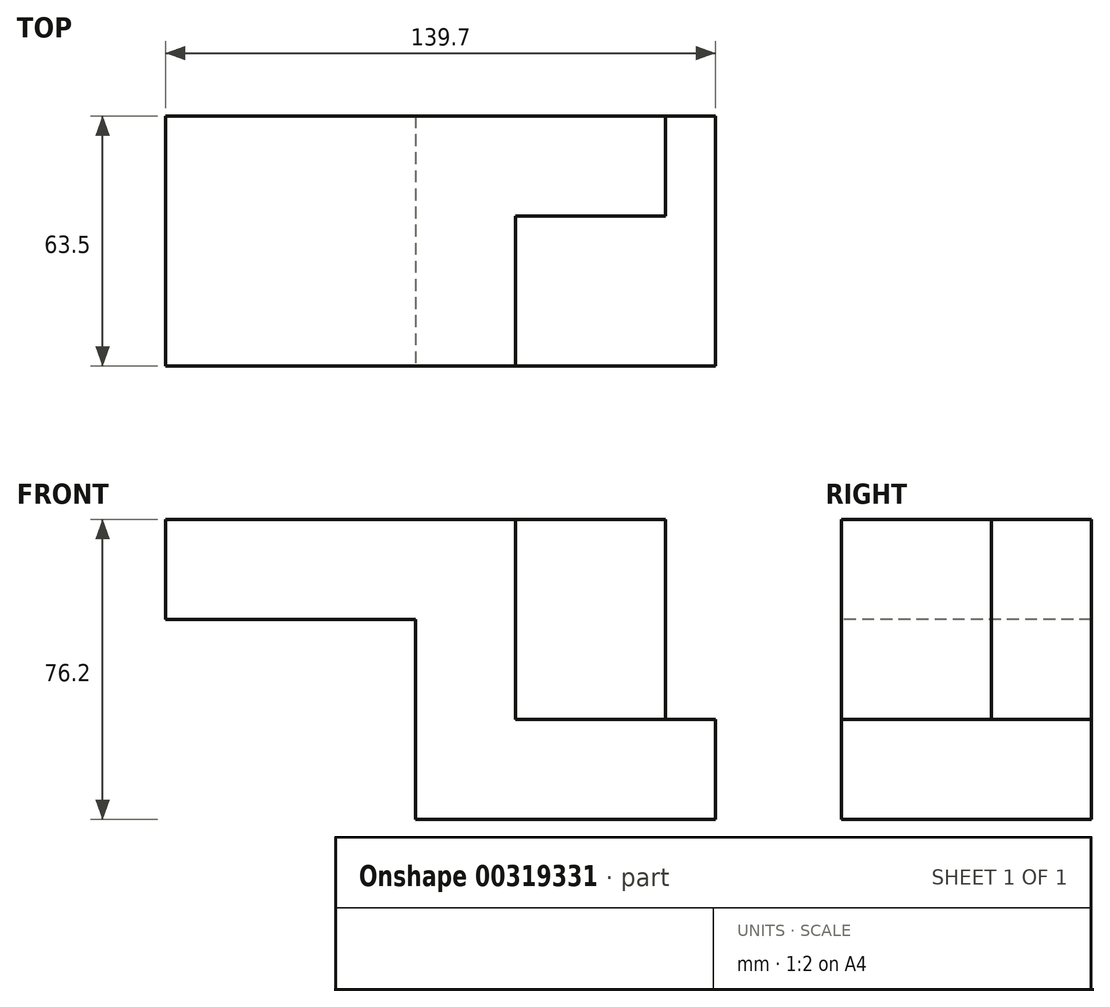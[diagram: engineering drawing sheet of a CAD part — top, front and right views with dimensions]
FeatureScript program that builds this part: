
annotation { "Feature Type Name" : "Feature", "Feature Type Description" : "" }
export const myFeature = defineFeature(function(context is Context, id is Id, definition is map)
    precondition{}
    {
        {
            var Q0;
            Q0=qCreatedBy(makeId("Top.planeOp"),FACE);
            var sketch = newSketch(context, id + "F0", { "sketchPlane" : qUnion([Q0])});
            skLineSegment(sketch, "E0.bottom", {"start": v(-37.29, 23.74) * mm, "end": v(38.91, 23.74) * mm});
            skLineSegment(sketch, "E0.top", {"start": v(-37.29, -39.76) * mm, "end": v(38.91, -39.76) * mm});
            skLineSegment(sketch, "E0.left", {"start": v(-37.29, 23.74) * mm, "end": v(-37.29, -39.76) * mm});
            skLineSegment(sketch, "E0.right", {"start": v(38.91, 23.74) * mm, "end": v(38.91, -39.76) * mm});
            skSolve(sketch);
        }
        {
            var Q0;
            Q0 = qSketchRegion(id + "F0", true);
            extrude(context, id + "F1", {"entities" : qUnion([Q0]), "depth" : 25.4 * mm});
        }
        {
            var Q0;
            Q0=makeQuery(id+"F1.opExtrude","CAP_FACE",FACE,{"disambiguationData":[OSD([sQuery(id+"F0.wireOp",EDGE,"E0.bottom"),sQuery(id+"F0.wireOp",EDGE,"E0.top"),sQuery(id+"F0.wireOp",EDGE,"E0.left"),sQuery(id+"F0.wireOp",EDGE,"E0.right")])],"isStart":false});
            var sketch = newSketch(context, id + "F2", { "sketchPlane" : qUnion([Q0])});
            skLineSegment(sketch, "E1", {"start": v(-37.29, -39.76) * mm, "end": v(-11.89, -39.76) * mm});
            skLineSegment(sketch, "E2", {"start": v(-11.89, -39.76) * mm, "end": v(-11.89, -1.66) * mm});
            skLineSegment(sketch, "E3", {"start": v(-11.89, -1.66) * mm, "end": v(26.21, -1.66) * mm});
            skLineSegment(sketch, "E4", {"start": v(26.21, -1.66) * mm, "end": v(26.21, 23.74) * mm});
            skLineSegment(sketch, "E5", {"start": v(26.21, 23.74) * mm, "end": v(-37.29, 23.74) * mm});
            skLineSegment(sketch, "E6", {"start": v(-37.29, 23.74) * mm, "end": v(-37.29, -39.76) * mm});
            skSolve(sketch);
        }
        {
            var Q0;
            Q0 = qSketchRegion(id + "F2", true);
            extrude(context, id + "F3", {"entities" : qUnion([Q0]), "operationType" : NewBodyOperationType.ADD, "depth" : 50.8 * mm});
        }
        {
            var Q0;
            Q0=makeQuery(id+"F3.boolean.opBoolean","MERGE",FACE,{"derivedFrom":[makeQuery(id+"F1.opExtrude","SWEPT_FACE",FACE,{"disambiguationData":[OSD([sQuery(id+"F0.wireOp",EDGE,"E0.left")])]}),makeQuery(id+"F3.opExtrude","SWEPT_FACE",FACE,{"disambiguationData":[OSD([sQuery(id+"F2.wireOp",EDGE,"E6")])]})]});
            var sketch = newSketch(context, id + "F4", { "sketchPlane" : qUnion([Q0])});
            skLineSegment(sketch, "E7", {"start": v(-23.74, 50.8) * mm, "end": v(39.76, 50.8) * mm});
            skLineSegment(sketch, "E8", {"start": v(39.76, 50.8) * mm, "end": v(39.76, 76.2) * mm});
            skLineSegment(sketch, "E9", {"start": v(39.76, 76.2) * mm, "end": v(-23.74, 76.2) * mm});
            skLineSegment(sketch, "E10", {"start": v(-23.74, 76.2) * mm, "end": v(-23.74, 50.8) * mm});
            skSolve(sketch);
        }
        {
            var Q0;
            Q0 = qSketchRegion(id + "F4", true);
            extrude(context, id + "F5", {"entities" : qUnion([Q0]), "operationType" : NewBodyOperationType.ADD, "depth" : 63.5 * mm});
        }
    });
